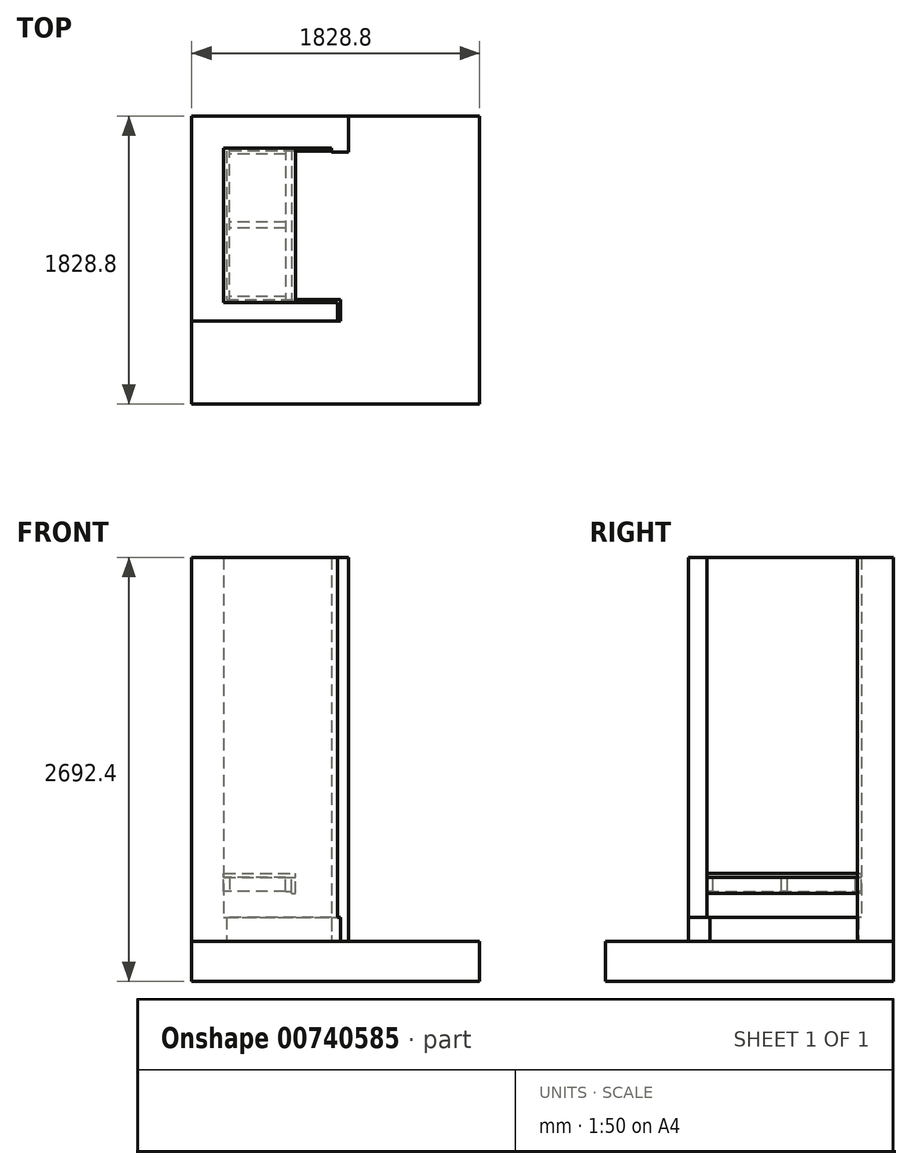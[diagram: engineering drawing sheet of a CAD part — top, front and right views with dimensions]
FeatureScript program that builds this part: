
annotation { "Feature Type Name" : "Feature", "Feature Type Description" : "" }
export const myFeature = defineFeature(function(context is Context, id is Id, definition is map)
    precondition{}
    {
        {
            var Q0;
            Q0=qCreatedBy(makeId("Top.planeOp"),FACE);
            var sketch = newSketch(context, id + "F0", { "sketchPlane" : qUnion([Q0])});
            skLineSegment(sketch, "E0", {"start": v(-107.95, 0) * mm, "end": v(-793.75, 0) * mm});
            skLineSegment(sketch, "E1", {"start": v(-793.75, 0) * mm, "end": v(-793.75, -981.08) * mm});
            skLineSegment(sketch, "E2", {"start": v(-793.75, -981.07) * mm, "end": v(-69.85, -981.07) * mm});
            skLineSegment(sketch, "E3", {"start": v(-69.85, -981.07) * mm, "end": v(-69.85, -1098.55) * mm});
            skLineSegment(sketch, "E4", {"start": v(-69.85, -1098.55) * mm, "end": v(-996.95, -1098.55) * mm});
            skLineSegment(sketch, "E5", {"start": v(-996.95, -1098.55) * mm, "end": v(-996.95, 203.2) * mm});
            skLineSegment(sketch, "E6", {"start": v(-996.95, 203.2) * mm, "end": v(0, 203.2) * mm});
            skLineSegment(sketch, "E7", {"start": v(0, 203.2) * mm, "end": v(0, 0) * mm});
            skLineSegment(sketch, "E8.top", {"start": v(0, -25.4) * mm, "end": v(-107.95, -25.4) * mm});
            skLineSegment(sketch, "E8.left", {"start": v(0, 0) * mm, "end": v(0, -25.4) * mm});
            skLineSegment(sketch, "E8.right", {"start": v(-107.95, 0) * mm, "end": v(-107.95, -25.4) * mm});
            skCircle(sketch, "E9", {"center": v(9.53, 0) * mm, "radius": 812.8 * mm, "construction": true});
            skSolve(sketch);
        }
        {
            var Q0;
            Q0=makeQuery(id+"F0.imprint","IMPRINT",FACE,{"disambiguationData":[TD([[makeQuery(id+"F0.imprint","IMPRINT",EDGE,{"derivedFrom":sQuery(id+"F0.wireOp",EDGE,"E0")}),-1.0]])]});
            extrude(context, id + "F1", {"entities" : qUnion([Q0]), "depth" : 2438.4 * mm, "offsetDistance" : 25.4 * mm});
        }
        {
            var Q0;
            Q0=makeQuery(id+"F1.opExtrude","CAP_FACE",FACE,{"disambiguationData":[OSD([sQuery(id+"F0.wireOp",EDGE,"E0"),sQuery(id+"F0.wireOp",EDGE,"E1"),sQuery(id+"F0.wireOp",EDGE,"E2"),sQuery(id+"F0.wireOp",EDGE,"E3"),sQuery(id+"F0.wireOp",EDGE,"E4"),sQuery(id+"F0.wireOp",EDGE,"E5"),sQuery(id+"F0.wireOp",EDGE,"E6"),sQuery(id+"F0.wireOp",EDGE,"E7"),sQuery(id+"F0.wireOp",EDGE,"E8.top"),sQuery(id+"F0.wireOp",EDGE,"E8.left"),sQuery(id+"F0.wireOp",EDGE,"E8.right")])],"isStart":true});
            var sketch = newSketch(context, id + "F2", { "sketchPlane" : qUnion([Q0])});
            skLineSegment(sketch, "E10.bottom", {"start": v(-996.95, -203.2) * mm, "end": v(831.85, -203.2) * mm});
            skLineSegment(sketch, "E10.top", {"start": v(-996.95, 1625.6) * mm, "end": v(831.85, 1625.6) * mm});
            skLineSegment(sketch, "E10.left", {"start": v(-996.95, -203.2) * mm, "end": v(-996.95, 1625.6) * mm});
            skLineSegment(sketch, "E10.right", {"start": v(831.85, -203.2) * mm, "end": v(831.85, 1625.6) * mm});
            skSolve(sketch);
        }
        {
            var Q0;
            {var subQ4=sQuery(id+"F2.wireOp",EDGE,"E10.top");Q0=makeQuery(id+"F2.imprint","IMPRINT",FACE,{"disambiguationData":[TD([[makeQuery(id+"F2.imprint","IMPRINT",EDGE,{"derivedFrom":subQ4}),-1.0]])]});}
            var Q1;
            Q1=makeQuery(id+"F2.imprint","IMPRINT",FACE,{"disambiguationData":[TD([[makeQuery(id+"F2.imprint","IMPRINT",EDGE,{"derivedFrom":makeQuery(id+"F1.opExtrude","CAP_EDGE",EDGE,{"disambiguationData":[OSD([sQuery(id+"F0.wireOp",EDGE,"E0")])],"isStart":true})}),1.0]])]});
            extrude(context, id + "F3", {"entities" : qUnion([Q0, Q1]), "depth" : 254 * mm, "offsetDistance" : 25.4 * mm});
        }
        {
            var Q0;
            Q0=makeQuery(id+"F3.opExtrude","CAP_FACE",FACE,{"disambiguationData":[OSD([sQuery(id+"F2.wireOp",EDGE,"E10.bottom"),sQuery(id+"F2.wireOp",EDGE,"E10.top"),sQuery(id+"F2.wireOp",EDGE,"E10.left"),sQuery(id+"F2.wireOp",EDGE,"E10.right")])],"isStart":true});
            var sketch = newSketch(context, id + "F4", { "sketchPlane" : qUnion([Q0])});
            skLineSegment(sketch, "E11.0", {"start": v(-793.75, -981.07) * mm, "end": v(-69.85, -981.07) * mm});
            skLineSegment(sketch, "E12.0", {"start": v(-793.75, 0) * mm, "end": v(-793.75, -981.08) * mm});
            skLineSegment(sketch, "E13.0", {"start": v(-69.85, -981.07) * mm, "end": v(-69.85, -1098.55) * mm});
            skLineSegment(sketch, "E14.0", {"start": v(-107.95, 0) * mm, "end": v(-793.75, 0) * mm});
            skLineSegment(sketch, "E15.0", {"start": v(-50.8, -962.02) * mm, "end": v(-50.8, -1098.55) * mm});
            skLineSegment(sketch, "E15.1", {"start": v(-774.7, -962.02) * mm, "end": v(-50.8, -962.02) * mm});
            skLineSegment(sketch, "E15.2", {"start": v(-774.7, -19.05) * mm, "end": v(-774.7, -962.02) * mm});
            skLineSegment(sketch, "E15.3", {"start": v(-107.95, -19.05) * mm, "end": v(-774.7, -19.05) * mm});
            skLineSegment(sketch, "E16", {"start": v(-69.85, -1098.55) * mm, "end": v(-50.8, -1098.55) * mm});
            skLineSegment(sketch, "E17", {"start": v(-107.95, 0) * mm, "end": v(-107.95, -19.05) * mm});
            skSolve(sketch);
        }
        {
            var Q0;
            Q0 = qSketchRegion(id + "F4", true);
            extrude(context, id + "F5", {"entities" : qUnion([Q0]), "operationType" : NewBodyOperationType.ADD, "depth" : 152.4 * mm, "offsetDistance" : 25.4 * mm});
        }
        {
            var Q0;
            Q0=makeQuery(id+"F3.opExtrude","CAP_FACE",FACE,{"disambiguationData":[OSD([sQuery(id+"F2.wireOp",EDGE,"E10.bottom"),sQuery(id+"F2.wireOp",EDGE,"E10.top"),sQuery(id+"F2.wireOp",EDGE,"E10.left"),sQuery(id+"F2.wireOp",EDGE,"E10.right")])],"isStart":true});
            cPlane(context, id + "F6", {"entities" : qUnion([Q0]), "cplaneType" : CPlaneType.OFFSET, "offset" : 431.8 * mm, "width" : 152.4 * mm, "height" : 152.4 * mm});
        }
        {
            var Q0;
            Q0=qCreatedBy(id+"F6.planeOp",FACE);
            var sketch = newSketch(context, id + "F7", { "sketchPlane" : qUnion([Q0])});
            skLineSegment(sketch, "E18.0.0", {"start": v(-793.75, -981.07) * mm, "end": v(-793.75, 0) * mm});
            skLineSegment(sketch, "E18.0.2", {"start": v(-793.75, 0) * mm, "end": v(-793.75, -981.08) * mm});
            skPoint(sketch, "E19.0.2.end.orphan", {"position": v(-69.85, -981.07) * mm});
            skPoint(sketch, "E20.0.2.start.orphan", {"position": v(-107.95, 0) * mm});
            skPoint(sketch, "E20.0.0.end.orphan", {"position": v(-107.95, 0) * mm});
            skPoint(sketch, "E19.0.0.start.orphan", {"position": v(-69.85, -981.07) * mm});
            skLineSegment(sketch, "E21.bottom", {"start": v(-793.75, -981.07) * mm, "end": v(-336.55, -981.07) * mm});
            skLineSegment(sketch, "E21.top", {"start": v(-793.75, 0) * mm, "end": v(-336.55, 0) * mm});
            skLineSegment(sketch, "E21.right", {"start": v(-336.55, -981.07) * mm, "end": v(-336.55, 0) * mm});
            skSolve(sketch);
        }
        {
            var Q0;
            Q0 = qSketchRegion(id + "F7", true);
            extrude(context, id + "F8", {"entities" : qUnion([Q0]), "oppositeDirection" : true, "depth" : 25.4 * mm, "offsetDistance" : 25.4 * mm});
        }
        {
            var Q0;
            Q0=makeQuery(id+"F1.opExtrude","SWEPT_FACE",FACE,{"disambiguationData":[OSD([sQuery(id+"F0.wireOp",EDGE,"E0")])]});
            var sketch = newSketch(context, id + "F9", { "sketchPlane" : qUnion([Q0])});
            skLineSegment(sketch, "E22.bottom", {"start": v(-793.75, 406.4) * mm, "end": v(-755.65, 406.4) * mm});
            skLineSegment(sketch, "E22.top", {"start": v(-793.75, 317.5) * mm, "end": v(-755.65, 317.5) * mm});
            skLineSegment(sketch, "E22.left", {"start": v(-793.75, 406.4) * mm, "end": v(-793.75, 317.5) * mm});
            skLineSegment(sketch, "E22.right", {"start": v(-755.65, 406.4) * mm, "end": v(-755.65, 317.5) * mm});
            skSolve(sketch);
        }
        {
            var Q0;
            Q0=makeQuery(id+"F9.imprint","IMPRINT",FACE,{"disambiguationData":[TD([[makeQuery(id+"F9.imprint","IMPRINT",EDGE,{"derivedFrom":sQuery(id+"F9.wireOp",EDGE,"E22.bottom")}),-1.0]])]});
            extrude(context, id + "F10", {"entities" : qUnion([Q0]), "endBound" : BoundingType.UP_TO_NEXT, "depth" : 25.4 * mm, "offsetDistance" : 25.4 * mm});
        }
        {
            var Q0;
            Q0=makeQuery(id+"F1.opExtrude","SWEPT_FACE",FACE,{"disambiguationData":[OSD([sQuery(id+"F0.wireOp",EDGE,"E2")])]});
            var sketch = newSketch(context, id + "F11", { "sketchPlane" : qUnion([Q0])});
            skLineSegment(sketch, "E23.bottom", {"start": v(336.55, 406.4) * mm, "end": v(361.95, 406.4) * mm});
            skLineSegment(sketch, "E23.top", {"start": v(336.55, 304.8) * mm, "end": v(361.95, 304.8) * mm});
            skLineSegment(sketch, "E23.left", {"start": v(336.55, 406.4) * mm, "end": v(336.55, 304.8) * mm});
            skLineSegment(sketch, "E23.right", {"start": v(361.95, 406.4) * mm, "end": v(361.95, 304.8) * mm});
            skSolve(sketch);
        }
        {
            var Q0;
            Q0=makeQuery(id+"F11.imprint","IMPRINT",FACE,{"disambiguationData":[TD([[makeQuery(id+"F11.imprint","IMPRINT",EDGE,{"derivedFrom":sQuery(id+"F11.wireOp",EDGE,"E23.bottom")}),1.0]])]});
            var sketch = newSketch(context, id + "F12", { "sketchPlane" : qUnion([Q0])});
            skLineSegment(sketch, "E24.bottom", {"start": v(361.95, 406.4) * mm, "end": v(400.05, 406.4) * mm});
            skLineSegment(sketch, "E24.top", {"start": v(361.95, 317.5) * mm, "end": v(400.05, 317.5) * mm});
            skLineSegment(sketch, "E24.left", {"start": v(361.95, 406.4) * mm, "end": v(361.95, 317.5) * mm});
            skLineSegment(sketch, "E24.right", {"start": v(400.05, 406.4) * mm, "end": v(400.05, 317.5) * mm});
            skSolve(sketch);
        }
        {
            var Q0;
            Q0 = qSketchRegion(id + "F12", true);
            extrude(context, id + "F13", {"entities" : qUnion([Q0]), "endBound" : BoundingType.UP_TO_NEXT, "depth" : 25.4 * mm, "offsetDistance" : 25.4 * mm});
        }
        {
            var Q0;
            Q0=makeQuery(id+"F11.imprint","IMPRINT",FACE,{"disambiguationData":[TD([[makeQuery(id+"F11.imprint","IMPRINT",EDGE,{"derivedFrom":sQuery(id+"F11.wireOp",EDGE,"E23.bottom")}),-1.0]])]});
            extrude(context, id + "F14", {"entities" : qUnion([Q0]), "endBound" : BoundingType.UP_TO_NEXT, "depth" : 25.4 * mm, "offsetDistance" : 25.4 * mm});
        }
        {
            var Q0;
            Q0=makeQuery(id+"F10.opExtrude","SWEPT_FACE",FACE,{"disambiguationData":[OSD([sQuery(id+"F9.wireOp",EDGE,"E22.right")])]});
            var sketch = newSketch(context, id + "F15", { "sketchPlane" : qUnion([Q0])});
            skLineSegment(sketch, "E25.bottom", {"start": v(0, 406.4) * mm, "end": v(-38.1, 406.4) * mm});
            skLineSegment(sketch, "E25.top", {"start": v(0, 317.5) * mm, "end": v(-38.1, 317.5) * mm});
            skLineSegment(sketch, "E25.left", {"start": v(0, 406.4) * mm, "end": v(0, 317.5) * mm});
            skLineSegment(sketch, "E25.right", {"start": v(-38.1, 406.4) * mm, "end": v(-38.1, 317.5) * mm});
            skLineSegment(sketch, "E26.bottom", {"start": v(-981.07, 406.4) * mm, "end": v(-942.97, 406.4) * mm});
            skLineSegment(sketch, "E26.top", {"start": v(-981.07, 317.5) * mm, "end": v(-942.97, 317.5) * mm});
            skLineSegment(sketch, "E26.left", {"start": v(-981.07, 406.4) * mm, "end": v(-981.07, 317.5) * mm});
            skLineSegment(sketch, "E26.right", {"start": v(-942.97, 406.4) * mm, "end": v(-942.97, 317.5) * mm});
            skLineSegment(sketch, "E27.bottom", {"start": v(-509.59, 406.4) * mm, "end": v(-471.49, 406.4) * mm});
            skLineSegment(sketch, "E27.top", {"start": v(-509.59, 317.5) * mm, "end": v(-471.49, 317.5) * mm});
            skLineSegment(sketch, "E27.left", {"start": v(-509.59, 406.4) * mm, "end": v(-509.59, 317.5) * mm});
            skLineSegment(sketch, "E27.right", {"start": v(-471.49, 406.4) * mm, "end": v(-471.49, 317.5) * mm});
            skLineSegment(sketch, "E28", {"start": v(-942.97, 361.95) * mm, "end": v(-509.59, 361.95) * mm, "construction": true});
            skLineSegment(sketch, "E29", {"start": v(-471.49, 361.95) * mm, "end": v(-38.1, 361.95) * mm, "construction": true});
            skSolve(sketch);
        }
        {
            var Q0;
            Q0=makeQuery(id+"F15.imprint","IMPRINT",FACE,{"disambiguationData":[TD([[makeQuery(id+"F15.imprint","IMPRINT",EDGE,{"derivedFrom":sQuery(id+"F15.wireOp",EDGE,"E26.bottom")}),-1.0]])]});
            var Q1;
            Q1=makeQuery(id+"F15.imprint","IMPRINT",FACE,{"disambiguationData":[TD([[makeQuery(id+"F15.imprint","IMPRINT",EDGE,{"derivedFrom":sQuery(id+"F15.wireOp",EDGE,"E27.bottom")}),-1.0]])]});
            var Q2;
            Q2=makeQuery(id+"F15.imprint","IMPRINT",FACE,{"disambiguationData":[TD([[makeQuery(id+"F15.imprint","IMPRINT",EDGE,{"derivedFrom":sQuery(id+"F15.wireOp",EDGE,"E25.bottom")}),-1.0]])]});
            extrude(context, id + "F16", {"entities" : qUnion([Q0, Q1, Q2]), "endBound" : BoundingType.UP_TO_NEXT, "depth" : 25.4 * mm, "offsetDistance" : 25.4 * mm});
        }
    });
